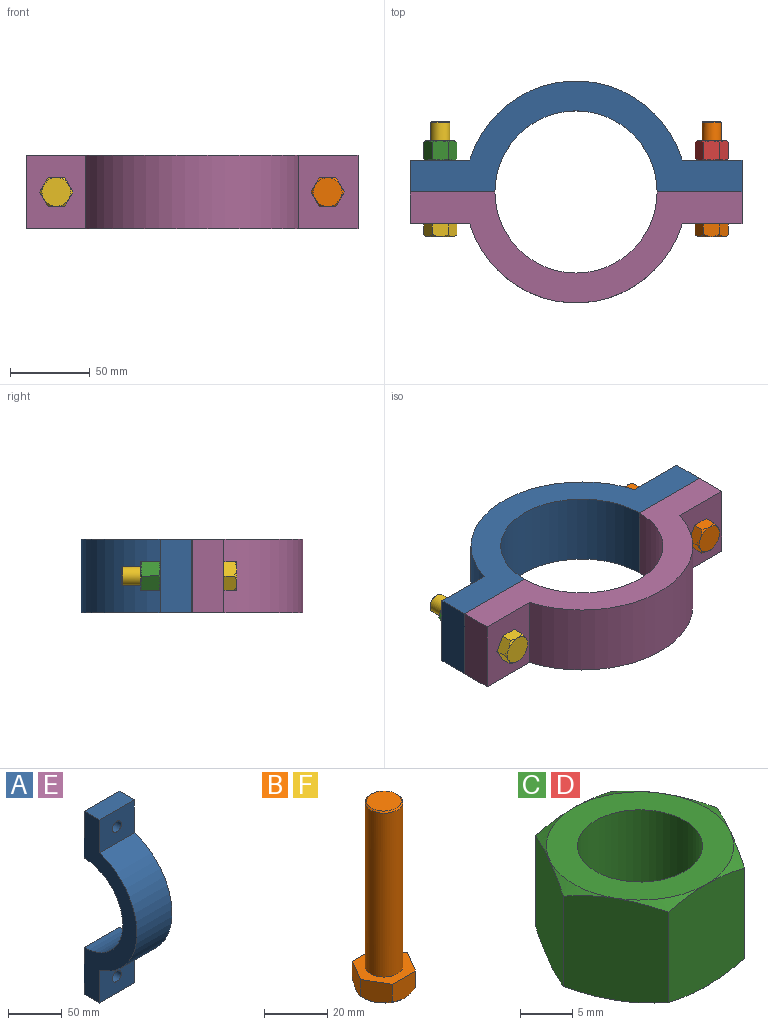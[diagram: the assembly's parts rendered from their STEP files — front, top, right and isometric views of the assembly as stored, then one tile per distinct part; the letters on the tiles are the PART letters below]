
ASSEMBLY  parts=6 mates=15
PART A: 12 faces, bbox 46x69.5x208 mm
  f0: cylinder r=6mm len=20mm, axis (0,1,0), area 754mm2, adj f3,f7
  f1: cylinder r=6mm len=20mm, axis (0,-1,0), area 754mm2, adj f6,f9
  f2: cylinder r=50.8mm len=101.6mm, axis (1,0,0), area 7341.3mm2, adj f3,f6,f8,f10
  f3: plane 53.2x46mm, normal (0,1,0), area 2334.1mm2, adj f0,f2,f4,f8,f10
  f4: plane 46x20mm, normal (0,0,-1), area 920mm2, adj f3,f7,f8,f10
  f5: plane 46x20mm, normal (0,0,1), area 920mm2, adj f6,f8,f9,f10
  f6: plane 53.2x46mm, normal (0,1,0), area 2334.1mm2, adj f1,f2,f5,f8,f10
  f7: plane 46x37.44mm, normal (0,-1,0), area 1609.1mm2, adj f0,f4,f8,f10,f11
  f8: plane 208x69.5mm, normal (1,0,0), area 4952.5mm2, adj f2,f3,f4,f5,f6,f7,f9,f11
  f9: plane 46x37.44mm, normal (0,-1,0), area 1609.1mm2, adj f1,f5,f8,f10,f11
  f10: plane 208x69.5mm, normal (-1,0,0), area 4952.5mm2, adj f2,f3,f4,f5,f6,f7,f9,f11
  f11: cylinder r=69.5mm len=133.12mm, axis (1,0,0), area 8177.3mm2, adj f7,f8,f9,f10
PART B: 12 faces, bbox 20.8x20.8x72 mm
  f0: plane 17.98x17.98mm, normal (0,0,-1), area 254mm2, adj f1
  f1: cone r=10.4mm half-angle=45deg, axis (0,0,1), area 37.6mm2, adj f0,f2,f3,f4,f5,f6,f7
  f2: plane 9x7.95mm, normal (-0.87,-0.5,0), area 77.6mm2, adj f1,f3,f7,f9
  f3: plane 10.39x7.95mm, normal (0,-1,0), area 77.6mm2, adj f1,f2,f4,f9
  f4: plane 9x7.95mm, normal (0.87,-0.5,0), area 77.6mm2, adj f1,f3,f5,f9
  f5: plane 9x7.95mm, normal (0.87,0.5,0), area 77.6mm2, adj f1,f4,f6,f9
  f6: plane 10.39x7.95mm, normal (0,1,0), area 77.6mm2, adj f1,f5,f7,f9
  f7: plane 9x7.95mm, normal (-0.87,0.5,0), area 77.6mm2, adj f1,f2,f6,f9
  f8: plane 11x11mm, normal (0,0,1), area 95mm2, adj f10
  f9: plane 20.78x18mm, normal (0,0,1), area 167.5mm2, adj f2,f3,f4,f5,f6,f7,f11
  f10: cone r=6mm half-angle=45deg, axis (0,0,-1), area 25.5mm2, adj f8,f11
  f11: cylinder r=6mm len=63.5mm, axis (0,0,1), area 2393.9mm2, adj f9,f10
PART C: 11 faces, bbox 20.8x20.8x12 mm
  f0: plane 12x9mm, normal (-0.87,-0.5,0), area 119.7mm2, adj f1,f5,f6,f7
  f1: plane 12x9mm, normal (-0.87,0.5,0), area 119.7mm2, adj f0,f2,f6,f7
  f2: plane 12x10.39mm, normal (0,1,0), area 119.7mm2, adj f1,f3,f6,f7
  f3: plane 12x9mm, normal (0.87,0.5,0), area 119.7mm2, adj f2,f4,f6,f7
  f4: plane 12x9mm, normal (0.87,-0.5,0), area 119.7mm2, adj f3,f5,f6,f7
  f5: plane 12x10.39mm, normal (0,-1,0), area 119.7mm2, adj f0,f4,f6,f7
  f6: cone r=10.4mm half-angle=63.4deg, axis (0,0,-1), area 29.7mm2, adj f0,f1,f2,f3,f4,f5,f8
  f7: cone r=10.4mm half-angle=63.4deg, axis (0,0,1), area 29.7mm2, adj f0,f1,f2,f3,f4,f5,f9
  f8: plane 17.98x17.98mm, normal (0,0,1), area 140.9mm2, adj f6,f10
  f9: plane 17.98x17.98mm, normal (0,0,-1), area 140.9mm2, adj f7,f10
  f10: cylinder r=6mm len=12mm, axis (0,0,1), area 452.4mm2, adj f8,f9
PART D: same geometry as C
PART E: same geometry as A
PART F: same geometry as B
PLACE A rot(axis=(0.71,0,-0.71),180deg) t=(-0.02,-43.5,9)mm
PLACE B rot(axis=(-1,0,0),90deg) t=(84.98,-63.5,9)mm
PLACE C rot(axis=(0,-0.71,-0.71),180deg) t=(-85.02,-23.5,9)mm
PLACE D rot(axis=(0,-0.71,-0.71),180deg) t=(84.98,-23.5,9)mm
PLACE E rot(axis=(0,1,0),90deg) t=(-0.02,-43.5,9)mm
PLACE F rot(axis=(0,0.71,0.71),180deg) t=(-85.02,-63.5,9)mm
MATE planar A.f6 <-> E.f3  axis (0,-1,0) through (-77.05,-43.5,9)mm
MATE parallel D.f5 <-> A.f8  axis (0,0,-1) through (84.98,-17.5,0)mm
MATE parallel B.f6 <-> E.f8  axis (0,0,-1) through (84.98,-67.24,0)mm
MATE cylindrical F.f1 <-> C.f6  axis (0,1,0) through (-85.02,-31.75,9)mm
MATE planar A.f9 <-> C.f6  axis (0,1,0) through (-85.32,-23.5,9)mm
MATE parallel A.f8 <-> C.f2  axis (0,0,-1) through (-85.3,-23.5,-14)mm
MATE cylindrical B.f1 <-> E.f1  axis (0,1,0) through (84.98,-31.75,9)mm
MATE cylindrical F.f1 <-> E.f0  axis (0,1,0) through (-85.02,0,9)mm
MATE planar E.f9 <-> B.f9  axis (0,-1,0) through (85.28,-63.5,9)mm
MATE planar E.f10 <-> A.f10  axis (0,0,1) through (-85.3,-63.5,32)mm
MATE parallel F.f3 <-> E.f8  axis (0,0,-1) through (-85.02,-67.24,0)mm
MATE planar E.f7 <-> F.f1  axis (0,-1,0) through (-104.02,-63.5,32)mm
MATE planar A.f4 <-> E.f5  axis (1,0,0) through (103.98,-23.5,9)mm
MATE cylindrical D.f6 <-> B.f1  axis (0,1,0) through (84.98,-11.5,9)mm
MATE planar D.f6 <-> A.f7  axis (0,-1,0) through (84.98,-23.5,9)mm
